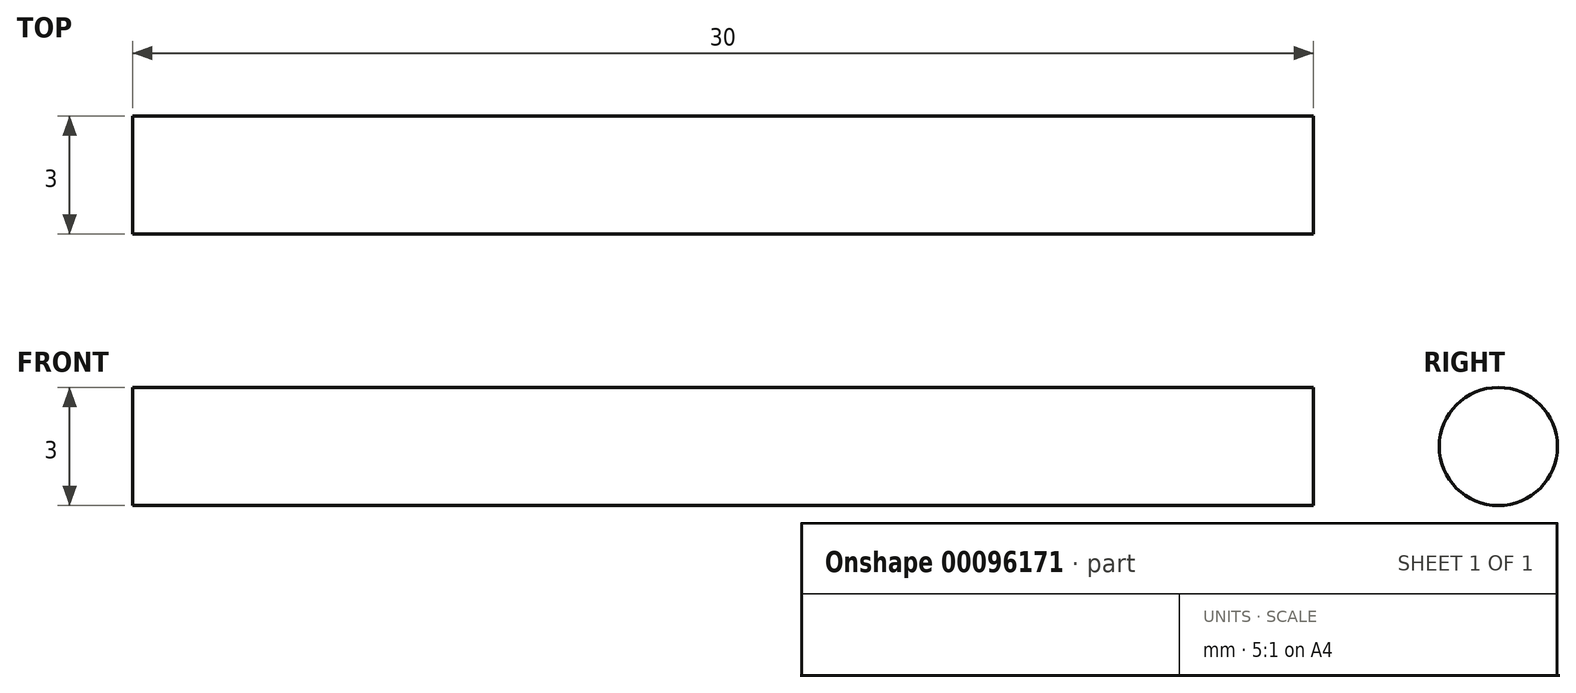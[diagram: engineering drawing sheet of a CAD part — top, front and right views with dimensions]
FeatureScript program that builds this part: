
annotation { "Feature Type Name" : "Feature", "Feature Type Description" : "" }
export const myFeature = defineFeature(function(context is Context, id is Id, definition is map)
    precondition{}
    {
        {
            var Q0;
            Q0=qCreatedBy(makeId("Right.planeOp"),FACE);
            var sketch = newSketch(context, id + "F0", { "sketchPlane" : qUnion([Q0])});
            skCircle(sketch, "E0", {"center": v(0, 0) * mm, "radius": 1.5 * mm});
            skSolve(sketch);
        }
        {
            var Q0;
            Q0 = qSketchRegion(id + "F0", true);
            extrude(context, id + "F1", {"entities" : qUnion([Q0]), "depth" : 15 * mm, "hasSecondDirection" : true, "secondDirectionOppositeDirection" : true, "secondDirectionDepth" : 15 * mm});
        }
    });
